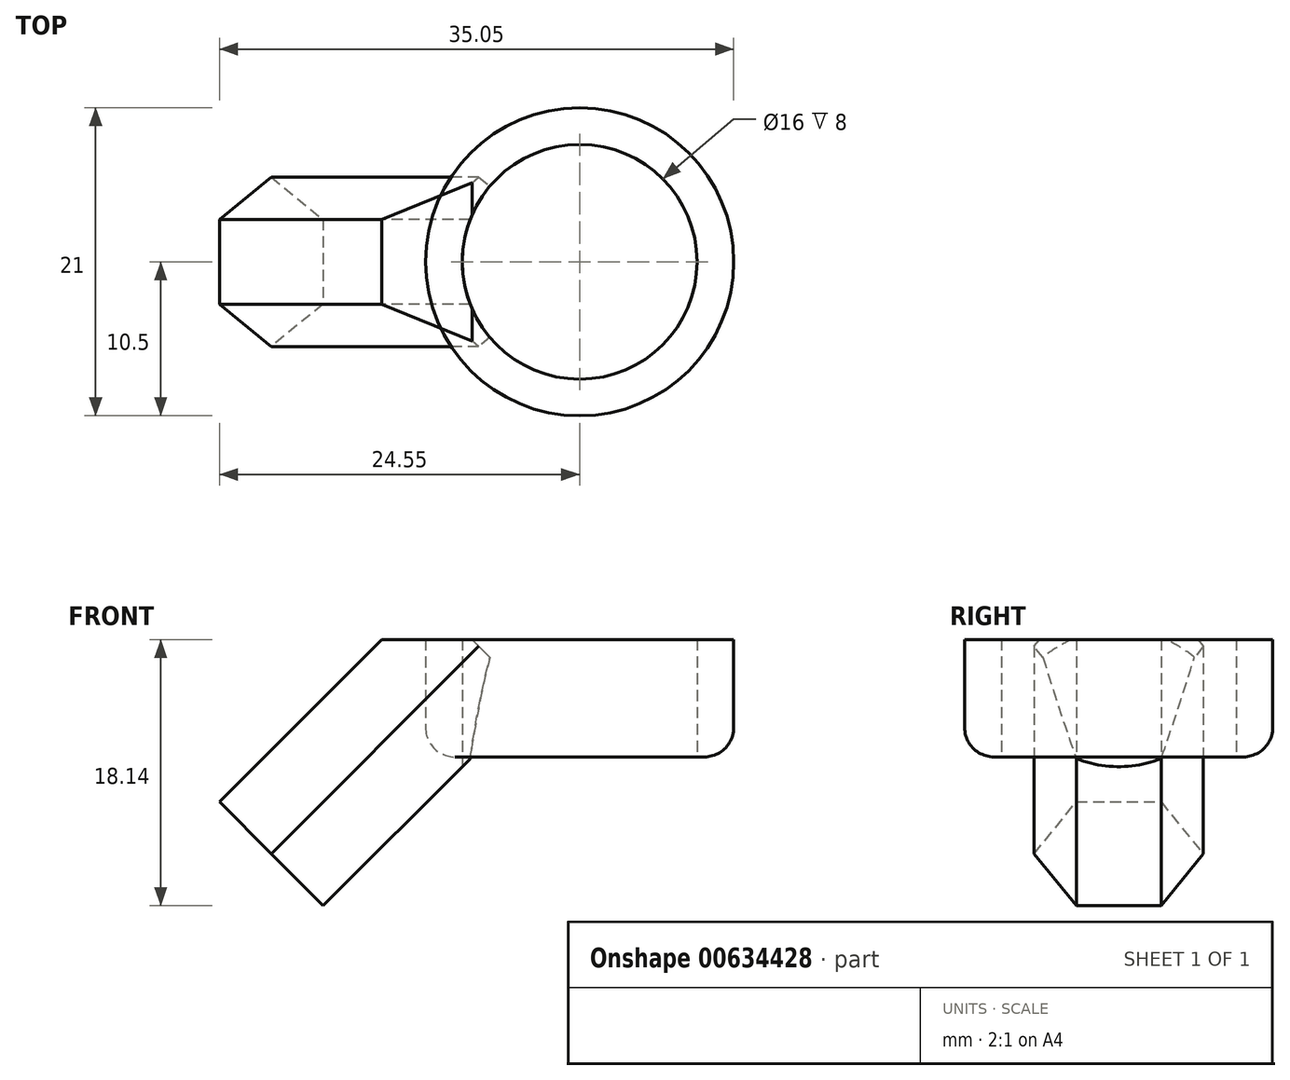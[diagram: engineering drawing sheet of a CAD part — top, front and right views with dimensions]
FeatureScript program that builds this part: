
annotation { "Feature Type Name" : "Feature", "Feature Type Description" : "" }
export const myFeature = defineFeature(function(context is Context, id is Id, definition is map)
    precondition{}
    {
        {
            var Q0;
            Q0=qCreatedBy(makeId("Top.planeOp"),FACE);
            var sketch = newSketch(context, id + "F0", { "sketchPlane" : qUnion([Q0])});
            skCircle(sketch, "E0", {"center": v(0, 0) * mm, "radius": 8 * mm});
            skCircle(sketch, "E1.0", {"center": v(0, 0) * mm, "radius": 10.5 * mm});
            skSolve(sketch);
        }
        {
            var Q0;
            Q0=makeQuery(id+"F0.imprint","IMPRINT",FACE,{"disambiguationData":[TD([[makeQuery(id+"F0.imprint","IMPRINT",EDGE,{"derivedFrom":sQuery(id+"F0.wireOp",EDGE,"E0")}),-1.0]])]});
            extrude(context, id + "F1", {"entities" : qUnion([Q0]), "depth" : 8 * mm, "offsetDistance" : 25 * mm});
        }
        {
            var Q0;
            Q0=makeQuery(id+"F1.opExtrude","CAP_EDGE",EDGE,{"disambiguationData":[OSD([sQuery(id+"F0.wireOp",EDGE,"E1.0")])],"isStart":true});
            fillet(context, id + "F2", {"entities" : qUnion([Q0]), "radius" : 2 * mm, "tangentPropagation" : true, "allowEdgeOverflow" : false});
        }
        {
            var Q0;
            Q0=qCreatedBy(makeId("Top.planeOp"),FACE);
            var sketch = newSketch(context, id + "F3", { "sketchPlane" : qUnion([Q0])});
            skCircle(sketch, "E2.cCircle", {"center": v(-13.33, 0) * mm, "radius": 5 * mm, "construction": true});
            skLineSegment(sketch, "E2.0", {"start": v(-8.33, 2.89) * mm, "end": v(-8.33, -2.89) * mm});
            skLineSegment(sketch, "E2.1", {"start": v(-8.33, -2.89) * mm, "end": v(-13.33, -5.77) * mm});
            skLineSegment(sketch, "E2.2", {"start": v(-13.33, -5.77) * mm, "end": v(-18.33, -2.89) * mm});
            skLineSegment(sketch, "E2.3", {"start": v(-18.33, -2.89) * mm, "end": v(-18.33, 2.89) * mm});
            skLineSegment(sketch, "E2.4", {"start": v(-18.33, 2.89) * mm, "end": v(-13.33, 5.77) * mm});
            skLineSegment(sketch, "E2.5", {"start": v(-13.33, 5.77) * mm, "end": v(-8.33, 2.89) * mm});
            skPoint(sketch, "E2.0.midPoint", {"position": v(-8.33, 0) * mm});
            skSolve(sketch);
        }
        {
            var Q0;
            Q0=qSketchRegion(id+"F3",true);
            extrude(context, id + "F4", {"entities" : qUnion([Q0]), "depth" : 4 * mm, "offsetDistance" : 25 * mm, "hasSecondDirection" : true, "secondDirectionOppositeDirection" : true, "secondDirectionDepth" : 16 * mm});
        }
        {
            var Q0;
            Q0=makeQuery(id+"F4.opExtrude","SWEPT_BODY",BODY,{"disambiguationData":[OSD([sQuery(id+"F3.wireOp",EDGE,"E2.0"),sQuery(id+"F3.wireOp",EDGE,"E2.1"),sQuery(id+"F3.wireOp",EDGE,"E2.2"),sQuery(id+"F3.wireOp",EDGE,"E2.3"),sQuery(id+"F3.wireOp",EDGE,"E2.4"),sQuery(id+"F3.wireOp",EDGE,"E2.5")])]});
            var Q1;
            Q1=makeQuery(id+"F4.opExtrude","CAP_EDGE",EDGE,{"disambiguationData":[OSD([sQuery(id+"F3.wireOp",EDGE,"E2.0")])],"isStart":false});
            transform(context, id + "F5", {"entities" : qUnion([Q0]), "transformType" : TransformType.ROTATION, "transformAxis" : qUnion([Q1]), "angle" : 45 * degree, "oppositeDirection" : true, "makeCopy" : false});
        }
        {
            var Q0;
            Q0=makeQuery(id+"F4.opExtrude","SWEPT_BODY",BODY,{"disambiguationData":[OSD([sQuery(id+"F3.wireOp",EDGE,"E2.0"),sQuery(id+"F3.wireOp",EDGE,"E2.1"),sQuery(id+"F3.wireOp",EDGE,"E2.2"),sQuery(id+"F3.wireOp",EDGE,"E2.3"),sQuery(id+"F3.wireOp",EDGE,"E2.4"),sQuery(id+"F3.wireOp",EDGE,"E2.5")])]});
            transform(context, id + "F6", {"entities" : qUnion([Q0]), "transformType" : TransformType.TRANSLATION_3D, "dx" : 5 * mm, "dy" : 0 * mm, "dz" : 0 * mm, "makeCopy" : false});
        }
        {
            var Q0;
            Q0=makeQuery(id+"F0.imprint","IMPRINT",FACE,{"disambiguationData":[TD([[makeQuery(id+"F0.imprint","IMPRINT",EDGE,{"derivedFrom":sQuery(id+"F0.wireOp",EDGE,"E0")}),1.0]])]});
            extrude(context, id + "F7", {"entities" : qUnion([Q0]), "operationType" : NewBodyOperationType.REMOVE, "depth" : 25 * mm, "offsetDistance" : 25 * mm, "hasSecondDirection" : true, "secondDirectionOppositeDirection" : true, "secondDirectionDepth" : 25 * mm});
        }
        {
            var Q0;
            Q0=makeQuery(id+"F1.opExtrude","CAP_FACE",FACE,{"disambiguationData":[OSD([sQuery(id+"F0.wireOp",EDGE,"E0"),sQuery(id+"F0.wireOp",EDGE,"E1.0")])],"isStart":false});
            var sketch = newSketch(context, id + "F8", { "sketchPlane" : qUnion([Q0])});
            skLineSegment(sketch, "E3.bottom", {"start": v(-22, -12.15) * mm, "end": v(4.12, -12.15) * mm});
            skLineSegment(sketch, "E3.top", {"start": v(-22, 16.16) * mm, "end": v(4.12, 16.16) * mm});
            skLineSegment(sketch, "E3.left", {"start": v(-22, -12.15) * mm, "end": v(-22, 16.16) * mm});
            skLineSegment(sketch, "E3.right", {"start": v(4.12, -12.15) * mm, "end": v(4.12, 16.16) * mm});
            skSolve(sketch);
        }
        {
            var Q0;
            Q0=qSketchRegion(id+"F8",true);
            extrude(context, id + "F9", {"entities" : qUnion([Q0]), "operationType" : NewBodyOperationType.REMOVE, "depth" : 25 * mm, "offsetDistance" : 25 * mm});
        }
    });
